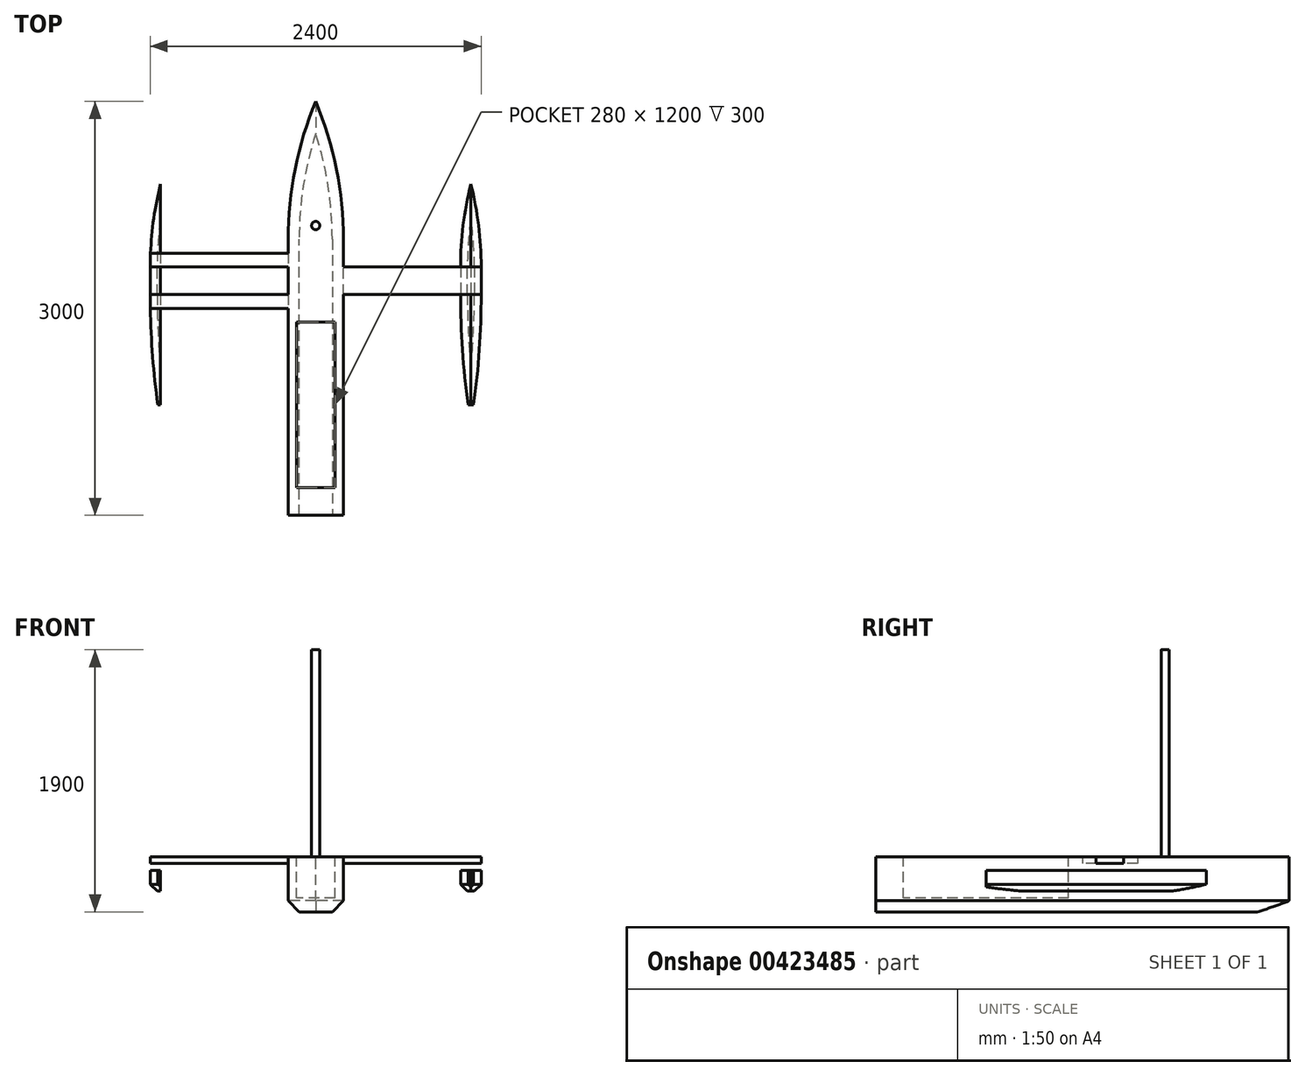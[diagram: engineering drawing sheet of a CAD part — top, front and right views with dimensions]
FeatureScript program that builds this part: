
annotation { "Feature Type Name" : "Feature", "Feature Type Description" : "" }
export const myFeature = defineFeature(function(context is Context, id is Id, definition is map)
    precondition{}
    {
        {
            var Q0;
            Q0=qCreatedBy(makeId("Top.planeOp"),FACE);
            var sketch = newSketch(context, id + "F0", { "sketchPlane" : qUnion([Q0])});
            skLineSegment(sketch, "E0", {"start": v(0, 0) * mm, "end": v(-200, 0) * mm});
            skLineSegment(sketch, "E1", {"start": v(0, 3000) * mm, "end": v(0, 0) * mm});
            skLineSegment(sketch, "E2", {"start": v(-200, 0) * mm, "end": v(-200, 2000) * mm});
            skArc(sketch, "E3", {"start": v(-200, 2000) * mm, "mid": v(-149.5, 2509.9) * mm, "end": v(0, 3000) * mm});
            skSolve(sketch);
        }
        {
            var Q0;
            Q0=makeQuery(id+"F0.imprint","IMPRINT",FACE,{"disambiguationData":[TD([[makeQuery(id+"F0.imprint","IMPRINT",EDGE,{"derivedFrom":sQuery(id+"F0.wireOp",EDGE,"E0")}),-1.0]])]});
            extrude(context, id + "F1", {"entities" : qUnion([Q0]), "oppositeDirection" : true, "depth" : 400 * mm});
        }
        {
            var Q0;
            Q0=makeQuery(id+"F1.opExtrude","SWEPT_BODY",BODY,{"disambiguationData":[OSD([sQuery(id+"F0.wireOp",EDGE,"E0"),sQuery(id+"F0.wireOp",EDGE,"E1"),sQuery(id+"F0.wireOp",EDGE,"E2"),sQuery(id+"F0.wireOp",EDGE,"E3")])]});
            var Q1;
            Q1=makeQuery(id+"F1.opExtrude","SWEPT_FACE",FACE,{"disambiguationData":[OSD([sQuery(id+"F0.wireOp",EDGE,"E1")])]});
            mirror(context, id + "F2", {"operationType" : NewBodyOperationType.ADD, "entities" : qUnion([Q0]), "mirrorPlane" : qUnion([Q1])});
        }
        {
            var Q0;
            Q0=qCreatedBy(makeId("Top.planeOp"),FACE);
            var sketch = newSketch(context, id + "F3", { "sketchPlane" : qUnion([Q0])});
            skLineSegment(sketch, "E4", {"start": v(-1200, 1500) * mm, "end": v(0, 1500) * mm});
            skLineSegment(sketch, "E5.0", {"start": v(-1200, 1600) * mm, "end": v(0, 1600) * mm});
            skLineSegment(sketch, "E6", {"start": v(-1200, 1600) * mm, "end": v(-1200, 1500) * mm});
            skLineSegment(sketch, "E7", {"start": v(0, 1600) * mm, "end": v(0, 1500) * mm});
            skLineSegment(sketch, "E8.0", {"start": v(-1200, 1800) * mm, "end": v(0, 1800) * mm});
            skLineSegment(sketch, "E9.0", {"start": v(-1200, 1900) * mm, "end": v(0, 1900) * mm});
            skLineSegment(sketch, "E10", {"start": v(-1200, 1900) * mm, "end": v(-1200, 1800) * mm});
            skLineSegment(sketch, "E11", {"start": v(0, 1900) * mm, "end": v(0, 1800) * mm});
            skSolve(sketch);
        }
        {
            var Q0;
            Q0 = qSketchRegion(id + "F3", true);
            extrude(context, id + "F4", {"entities" : qUnion([Q0]), "operationType" : NewBodyOperationType.ADD, "oppositeDirection" : true, "depth" : 50 * mm});
        }
        {
            var Q0;
            {var subQ0=makeQuery(id+"F1.opExtrude","CAP_FACE",FACE,{"disambiguationData":[OSD([sQuery(id+"F0.wireOp",EDGE,"E0"),sQuery(id+"F0.wireOp",EDGE,"E1"),sQuery(id+"F0.wireOp",EDGE,"E2"),sQuery(id+"F0.wireOp",EDGE,"E3")])],"isStart":true});Q0=makeQuery(id+"F4.boolean.opBoolean","MERGE",FACE,{"derivedFrom":[makeQuery(id+"F2.boolean.opBoolean","MERGE",FACE,{"derivedFrom":[subQ0,makeQuery(id+"F2.opPattern","COPY",FACE,{"derivedFrom":subQ0,"instanceName":"1"})]}),makeQuery(id+"F4.opExtrude","CAP_FACE",FACE,{"disambiguationData":[OSD([sQuery(id+"F3.wireOp",EDGE,"E4"),sQuery(id+"F3.wireOp",EDGE,"E5.0"),sQuery(id+"F3.wireOp",EDGE,"E6"),sQuery(id+"F3.wireOp",EDGE,"E7")])],"isStart":true}),makeQuery(id+"F4.opExtrude","CAP_FACE",FACE,{"disambiguationData":[OSD([sQuery(id+"F3.wireOp",EDGE,"E8.0"),sQuery(id+"F3.wireOp",EDGE,"E9.0"),sQuery(id+"F3.wireOp",EDGE,"E10"),sQuery(id+"F3.wireOp",EDGE,"E11")])],"isStart":true})]});}
            var sketch = newSketch(context, id + "F5", { "sketchPlane" : qUnion([Q0])});
            skLineSegment(sketch, "E12.0", {"start": v(-200, 1600) * mm, "end": v(-200, 1800) * mm});
            skLineSegment(sketch, "E13", {"start": v(-200, 1800) * mm, "end": v(1200, 1800) * mm});
            skLineSegment(sketch, "E14.0", {"start": v(-200, 1600) * mm, "end": v(1200, 1600) * mm});
            skLineSegment(sketch, "E15", {"start": v(1200, 1800) * mm, "end": v(1200, 1600) * mm});
            skSolve(sketch);
        }
        {
            var Q0;
            {var subQ0=sQuery(id+"F5.wireOp",EDGE,"E15");Q0=makeQuery(id+"F5.imprint","IMPRINT",FACE,{"disambiguationData":[TD([[makeQuery(id+"F5.imprint","IMPRINT",EDGE,{"derivedFrom":subQ0}),-1.0]])]});}
            extrude(context, id + "F6", {"entities" : qUnion([Q0]), "operationType" : NewBodyOperationType.ADD, "oppositeDirection" : true, "depth" : 50 * mm});
        }
        {
            var Q0;
            Q0=qCreatedBy(makeId("Top.planeOp"),FACE);
            var sketch = newSketch(context, id + "F7", { "sketchPlane" : qUnion([Q0])});
            skLineSegment(sketch, "E16.0", {"start": v(1200, 1800) * mm, "end": v(1200, 1600) * mm});
            skPoint(sketch, "E17", {"position": v(1125, 2400) * mm});
            skLineSegment(sketch, "E18", {"start": v(1125, 800) * mm, "end": v(1145, 800) * mm});
            skLineSegment(sketch, "E19", {"start": v(1125, 2400) * mm, "end": v(1125, 800) * mm});
            skArc(sketch, "E20", {"start": v(1200, 1800) * mm, "mid": v(1181.18, 2102.33) * mm, "end": v(1125, 2400) * mm});
            skArc(sketch, "E21", {"start": v(1200, 1600) * mm, "mid": v(1186.23, 1199.06) * mm, "end": v(1145, 800) * mm});
            skSolve(sketch);
        }
        {
            var Q0;
            Q0=makeQuery(id+"F7.imprint","IMPRINT",FACE,{"disambiguationData":[TD([[makeQuery(id+"F7.imprint","IMPRINT",EDGE,{"derivedFrom":sQuery(id+"F7.wireOp",EDGE,"E16.0")}),-1.0]])]});
            extrude(context, id + "F8", {"entities" : qUnion([Q0]), "oppositeDirection" : true, "depth" : 250 * mm, "hasSecondDirection" : true, "secondDirectionOppositeDirection" : true, "secondDirectionDepth" : 100 * mm});
        }
        {
            var Q0;
            Q0=makeQuery(id+"F8.opExtrude","SWEPT_BODY",BODY,{"disambiguationData":[OSD([sQuery(id+"F7.wireOp",EDGE,"E16.0"),sQuery(id+"F7.wireOp",EDGE,"E18"),sQuery(id+"F7.wireOp",EDGE,"E19"),sQuery(id+"F7.wireOp",EDGE,"E20"),sQuery(id+"F7.wireOp",EDGE,"E21")])]});
            var Q1;
            Q1=makeQuery(id+"F8.opExtrude","SWEPT_FACE",FACE,{"disambiguationData":[OSD([sQuery(id+"F7.wireOp",EDGE,"E19")])]});
            mirror(context, id + "F9", {"operationType" : NewBodyOperationType.ADD, "entities" : qUnion([Q0]), "mirrorPlane" : qUnion([Q1])});
        }
        {
            var Q0;
            Q0=makeQuery(id+"F8.opExtrude","SWEPT_BODY",BODY,{"disambiguationData":[OSD([sQuery(id+"F7.wireOp",EDGE,"E16.0"),sQuery(id+"F7.wireOp",EDGE,"E18"),sQuery(id+"F7.wireOp",EDGE,"E19"),sQuery(id+"F7.wireOp",EDGE,"E20"),sQuery(id+"F7.wireOp",EDGE,"E21")])]});
            var Q1;
            Q1=qCreatedBy(makeId("Right.planeOp"),FACE);
            mirror(context, id + "F10", {"entities" : qUnion([Q0]), "mirrorPlane" : qUnion([Q1])});
        }
        {
            var Q0;
            Q0=makeQuery(id+"F1.opExtrude","CAP_EDGE",EDGE,{"disambiguationData":[OSD([sQuery(id+"F0.wireOp",EDGE,"E2")])],"isStart":false});
            var Q1;
            Q1=makeQuery(id+"F1.opExtrude","CAP_EDGE",EDGE,{"disambiguationData":[OSD([sQuery(id+"F0.wireOp",EDGE,"E3")])],"isStart":false});
            var Q2;
            Q2=makeQuery(id+"F2.opPattern","COPY",EDGE,{"derivedFrom":makeQuery(id+"F1.opExtrude","CAP_EDGE",EDGE,{"disambiguationData":[OSD([sQuery(id+"F0.wireOp",EDGE,"E3")])],"isStart":false}),"instanceName":"1"});
            var Q3;
            Q3=makeQuery(id+"F2.opPattern","COPY",EDGE,{"derivedFrom":makeQuery(id+"F1.opExtrude","CAP_EDGE",EDGE,{"disambiguationData":[OSD([sQuery(id+"F0.wireOp",EDGE,"E2")])],"isStart":false}),"instanceName":"1"});
            chamfer(context, id + "F11", {"entities" : qUnion([Q0, Q1, Q2, Q3]), "width" : 80 * mm, "tangentPropagation" : true});
        }
        {
            var Q0;
            {var subQ0=sQuery(id+"F0.wireOp",EDGE,"E2");var subQ1=makeQuery(id+"F1.opExtrude","CAP_FACE",FACE,{"disambiguationData":[OSD([sQuery(id+"F0.wireOp",EDGE,"E0"),sQuery(id+"F0.wireOp",EDGE,"E1"),subQ0,sQuery(id+"F0.wireOp",EDGE,"E3")])],"isStart":true});Q0=makeQuery(id+"F6.boolean.opBoolean","MERGE",FACE,{"derivedFrom":[makeQuery(id+"F4.boolean.opBoolean","MERGE",FACE,{"derivedFrom":[makeQuery(id+"F2.boolean.opBoolean","MERGE",FACE,{"derivedFrom":[subQ1,makeQuery(id+"F2.opPattern","COPY",FACE,{"derivedFrom":subQ1,"instanceName":"1"})]}),makeQuery(id+"F4.opExtrude","CAP_FACE",FACE,{"disambiguationData":[OSD([sQuery(id+"F3.wireOp",EDGE,"E4"),sQuery(id+"F3.wireOp",EDGE,"E5.0"),sQuery(id+"F3.wireOp",EDGE,"E6"),sQuery(id+"F3.wireOp",EDGE,"E7")])],"isStart":true}),makeQuery(id+"F4.opExtrude","CAP_FACE",FACE,{"disambiguationData":[OSD([sQuery(id+"F3.wireOp",EDGE,"E8.0"),sQuery(id+"F3.wireOp",EDGE,"E9.0"),sQuery(id+"F3.wireOp",EDGE,"E10"),sQuery(id+"F3.wireOp",EDGE,"E11")])],"isStart":true})]}),makeQuery(id+"F6.opExtrude","CAP_FACE",FACE,{"disambiguationData":[OSD([subQ0,sQuery(id+"F5.wireOp",EDGE,"E13"),sQuery(id+"F5.wireOp",EDGE,"E14.0"),sQuery(id+"F5.wireOp",EDGE,"E15")])],"isStart":true})]});}
            var sketch = newSketch(context, id + "F12", { "sketchPlane" : qUnion([Q0])});
            skLineSegment(sketch, "E22.bottom", {"start": v(140, 1400) * mm, "end": v(0, 1400) * mm});
            skLineSegment(sketch, "E22.top", {"start": v(140, 200) * mm, "end": v(0, 200) * mm});
            skLineSegment(sketch, "E22.left", {"start": v(140, 1400) * mm, "end": v(140, 200) * mm});
            skLineSegment(sketch, "E22.right", {"start": v(0, 1400) * mm, "end": v(0, 200) * mm, "construction": true});
            skLineSegment(sketch, "E23.0", {"start": v(-140, 1400) * mm, "end": v(-140, 200) * mm});
            skLineSegment(sketch, "E24", {"start": v(-140, 1400) * mm, "end": v(0, 1400) * mm});
            skLineSegment(sketch, "E25", {"start": v(-140, 200) * mm, "end": v(0, 200) * mm});
            skSolve(sketch);
        }
        {
            var Q0;
            Q0 = qSketchRegion(id + "F12", true);
            extrude(context, id + "F13", {"entities" : qUnion([Q0]), "operationType" : NewBodyOperationType.REMOVE, "oppositeDirection" : true, "depth" : 300 * mm});
        }
        {
            var Q0;
            Q0=makeQuery(id+"F12.imprint","IMPRINT",FACE,{"disambiguationData":[TD([[makeQuery(id+"F12.imprint","IMPRINT",EDGE,{"derivedFrom":sQuery(id+"F12.wireOp",EDGE,"E22.bottom")}),-1.0]])]});
            var sketch = newSketch(context, id + "F14", { "sketchPlane" : qUnion([Q0])});
            skCircle(sketch, "E26", {"center": v(0, 2100) * mm, "radius": 30 * mm});
            skSolve(sketch);
        }
        {
            var Q0;
            Q0 = qSketchRegion(id + "F14", true);
            extrude(context, id + "F15", {"entities" : qUnion([Q0]), "operationType" : NewBodyOperationType.ADD, "depth" : 1500 * mm});
        }
        {
            var Q0;
            Q0=makeQuery(id+"F8.opExtrude","CAP_EDGE",EDGE,{"disambiguationData":[OSD([sQuery(id+"F7.wireOp",EDGE,"E20")])],"isStart":false});
            var Q1;
            Q1=makeQuery(id+"F9.opPattern","COPY",EDGE,{"derivedFrom":makeQuery(id+"F8.opExtrude","CAP_EDGE",EDGE,{"disambiguationData":[OSD([sQuery(id+"F7.wireOp",EDGE,"E20")])],"isStart":false}),"instanceName":"1"});
            chamfer(context, id + "F16", {"entities" : qUnion([Q0, Q1]), "width" : 50 * mm, "tangentPropagation" : true});
        }
        {
            var Q0;
            Q0=makeQuery(id+"F10.opPattern","COPY",EDGE,{"derivedFrom":makeQuery(id+"F8.opExtrude","CAP_EDGE",EDGE,{"disambiguationData":[OSD([sQuery(id+"F7.wireOp",EDGE,"E20")])],"isStart":false}),"instanceName":"1"});
            var Q1;
            Q1=makeQuery(id+"F10.opPattern","COPY",EDGE,{"derivedFrom":makeQuery(id+"F9.opPattern","COPY",EDGE,{"derivedFrom":makeQuery(id+"F8.opExtrude","CAP_EDGE",EDGE,{"disambiguationData":[OSD([sQuery(id+"F7.wireOp",EDGE,"E20")])],"isStart":false}),"instanceName":"1"}),"instanceName":"1"});
            chamfer(context, id + "F17", {"entities" : qUnion([Q0, Q1]), "width" : 50 * mm, "tangentPropagation" : true});
        }
    });
